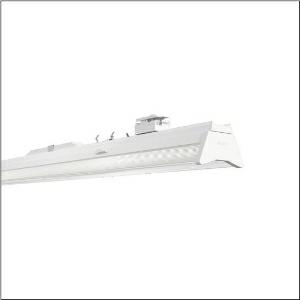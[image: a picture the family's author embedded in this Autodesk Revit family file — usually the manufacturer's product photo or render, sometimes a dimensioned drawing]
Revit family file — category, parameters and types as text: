
# Revit family: licross_r__21_performance_mo_51td16vn465g_a773
name_source: partatom
category: Lighting Fixtures
units: mm (PartAtom-declared; Revit-internal decimal feet)

## family parameters
Cut with Voids When Loaded = No
Host = Face
Light Source = No
Part Type = Normal
Room Calculation Point = No
Round Connector Dimension = Use Diameter
Shared = No

## types (1)
- --- (1 x LED, 6500 lm, 34.9 W, 4000K)
    Apparent Load = 35 VA
    CIE Flux Codes = 66 88 96 79 100
    Color Rendering = 80
    Color Temperature = 4000K
    Default Elevation = 1800 mm
    Description = Licross® 21 Performance MO, luminaire insert, of sheet steel, galvanised, coil coated, white, length: 1.500mm, width: 120mm, height: 123mm, LED rated luminous flux: 6.500lm, light colour: 840, control gear: DALI 2, CLO, with plug, 5-pole, with phase selection, mains connection: 220..240V, AC, 50/60Hz, start of lifetime: 35W, end of service life: 38W, internal wiring halogen-free, primary light control with lens, of plastic, primary optical cover: cover, of PMMA, light emission: direct/indirect distribution, primary light characteristic: symmetric, protection rating (complete): IP54, insulation class (complete): insulation class I (protective earthing), certification: CE, ENEC, VDE, UKCA, protection symbol: D if used in an environment with non-conductive dust loads with corresponding accessories, impact resistance: IK06, permissible ambient temperature for indoor applications: -25..+40°C, corresponds to IFS (International Featured Standards) requirements for safety and quality in the food industry, reducing of maximum allowable ambient temperature of 5°C with ceiling mounting, LABS conformity tested according to VDMA 24364:2018-05, packaging unit: 1 piece
    Height = 114 mm
    Lamp = 1 x LED
    Lamp Light Flux = 6500 lm
    Lamp Power = 34.9 W
    Lamp count = 1
    Length = 1500 mm
    Luminous efficacy = 186 lm/W
    Manufacturer = Siteco
    ModVariant = No
    Model = 51TD16VN465G
    Mounting Place = Ceiling
    Mounting Type = Pendant
    Number of Poles = 1
    OnlyDefault = Yes
    Power Factor = 1
    Product Name = Licross® 21 Performance MO
    Product group = luminaire insert | ceiling pendant
    ProductGroupID = 902
    Protection Class = Protection class I
    Protection Degree = IP 54
    RLX_Detail_Level = 1
    RLX_Emergency_Light_Flux = 0 lm
    RLX_Emergency_Type = 0
    RLX_Emergency_Type_DB = No
    RlxData = <blob elided: 34025 chars, md5=191bdcf2>
    Socket = socket
    Standby Power = 0 W
    System Light Flux = 6500 lm
    System Power = 35 W
    Type Comments = factory setting: luminous flux: 100 % | dim-lin: 254 | 236 mA
    Type Image = l_1256138.jpg
    URL = http://relux.com
    VarID = @adj_109331
    Voltage = 0 V
    Weight = 0.00 kg
    Width = 120 mm

## geometry (parser evidence)
native form markers: Blend x4, Sweep x12
no freeform markers — native parametric forms only
